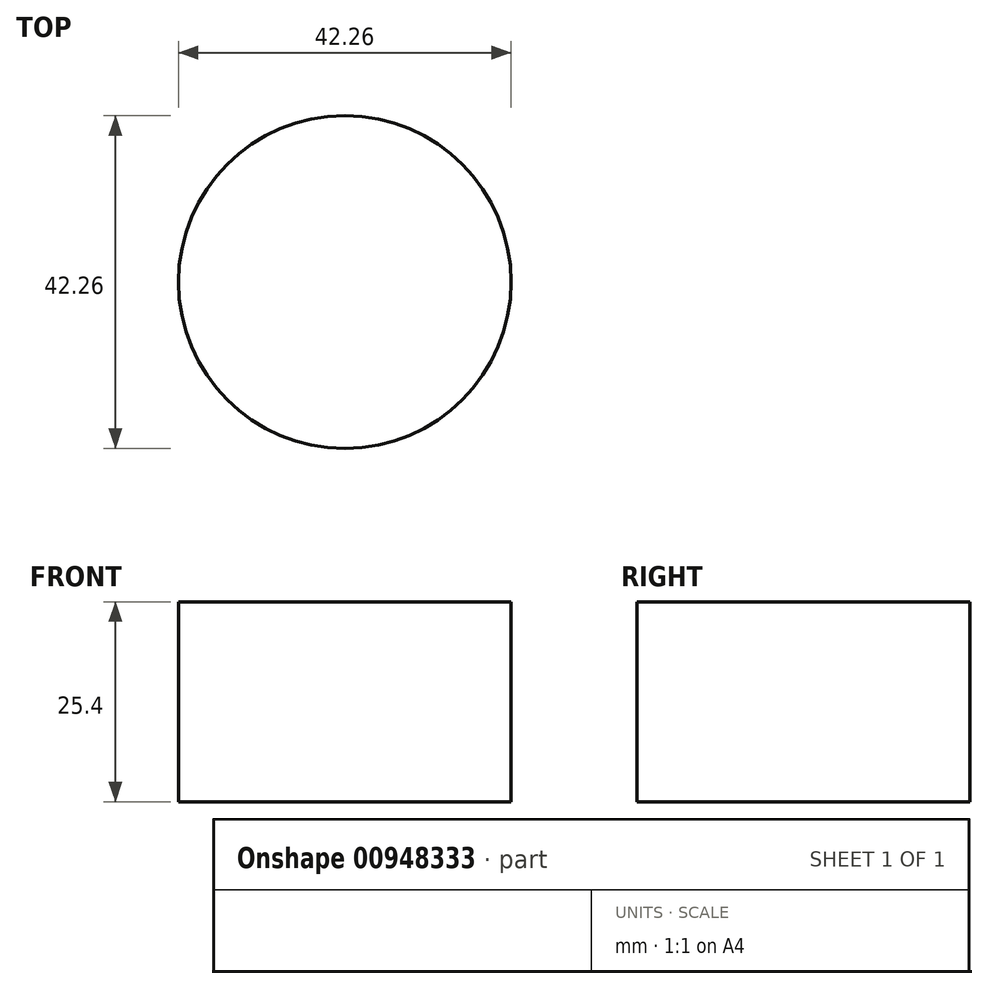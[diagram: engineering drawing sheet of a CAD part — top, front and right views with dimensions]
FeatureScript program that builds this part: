
annotation { "Feature Type Name" : "Feature", "Feature Type Description" : "" }
export const myFeature = defineFeature(function(context is Context, id is Id, definition is map)
    precondition{}
    {
        {
            var Q0;
            Q0=qCreatedBy(makeId("Top.planeOp"),FACE);
            var sketch = newSketch(context, id + "F0", { "sketchPlane" : qUnion([Q0])});
            skCircle(sketch, "E0", {"center": v(0, 0) * mm, "radius": 14.78 * mm, "construction": true});
            skSolve(sketch);
        }
        {
            var Q0;
            Q0=qCreatedBy(makeId("Top.planeOp"),FACE);
            var sketch = newSketch(context, id + "F1", { "sketchPlane" : qUnion([Q0])});
            skCircle(sketch, "E1.0", {"center": v(0, 0) * mm, "radius": 21.13 * mm});
            skSolve(sketch);
        }
        {
            var Q0;
            Q0=qCreatedBy(makeId("Top.planeOp"),FACE);
            var sketch = newSketch(context, id + "F2", { "sketchPlane" : qUnion([Q0])});
            skArc(sketch, "E2", {"start": v(9.3, 18.96) * mm, "mid": v(-0.6, 30.34) * mm, "end": v(-10.24, 18.75) * mm});
            skSolve(sketch);
        }
        {
            var Q0;
            Q0 = qSketchRegion(id + "F1", true);
            extrude(context, id + "F3", {"entities" : qUnion([Q0]), "depth" : 25.4 * mm, "offsetDistance" : 25.4 * mm});
        }
    });
